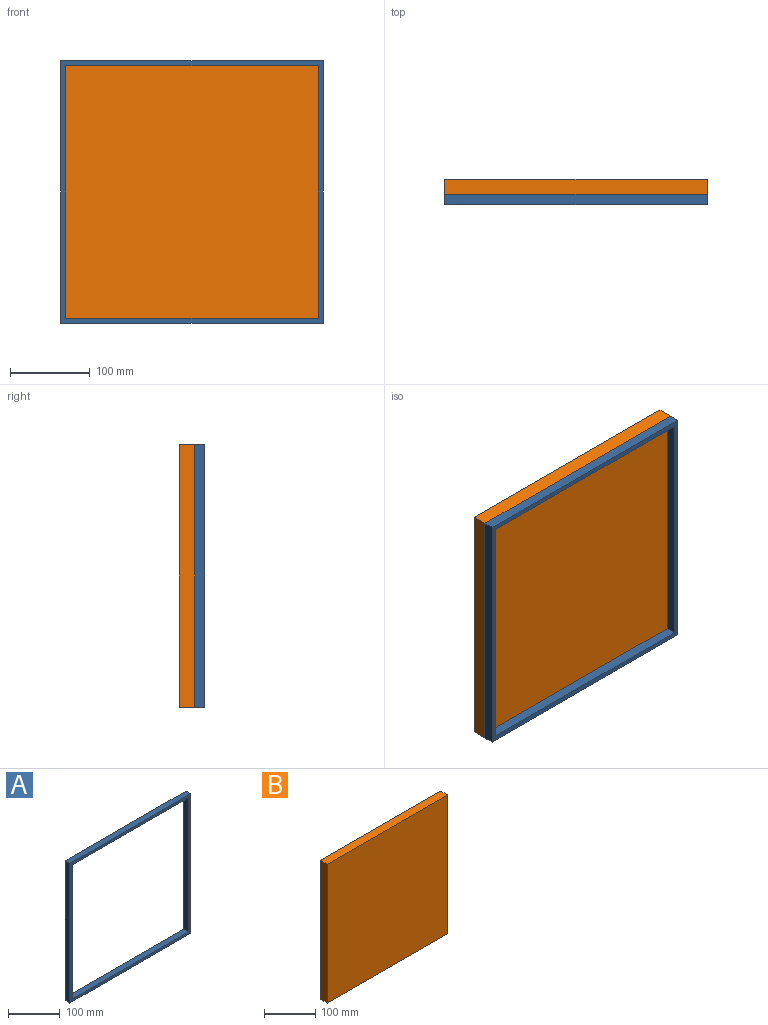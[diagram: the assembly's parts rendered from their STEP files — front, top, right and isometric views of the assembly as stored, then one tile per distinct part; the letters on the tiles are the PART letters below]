
ASSEMBLY  parts=2 mates=1
PART A: 10 faces, bbox 330.2x12.7x330.2 mm
  f0: plane 317.5x12.7mm, normal (0,0,1), area 4032.3mm2, adj f1,f7,f8,f9
  f1: plane 317.5x12.7mm, normal (1,0,0), area 4032.3mm2, adj f0,f2,f8,f9
  f2: plane 317.5x12.7mm, normal (0,0,-1), area 4032.3mm2, adj f1,f7,f8,f9
  f3: plane 330.2x12.7mm, normal (0,0,-1), area 4193.5mm2, adj f4,f6,f8,f9
  f4: plane 330.2x12.7mm, normal (1,0,0), area 4193.5mm2, adj f3,f5,f8,f9
  f5: plane 330.2x12.7mm, normal (0,0,1), area 4193.5mm2, adj f4,f6,f8,f9
  f6: plane 330.2x12.7mm, normal (-1,0,0), area 4193.5mm2, adj f3,f5,f8,f9
  f7: plane 317.5x12.7mm, normal (-1,0,0), area 4032.3mm2, adj f0,f2,f8,f9
  f8: plane 330.2x330.2mm, normal (0,-1,0), area 8225.8mm2, adj f0,f1,f2,f3,f4,f5,f6,f7
  f9: plane 330.2x330.2mm, normal (0,1,0), area 8225.8mm2, adj f0,f1,f2,f3,f4,f5,f6,f7
PART B: 6 faces, bbox 330.2x19.1x330.2 mm
  f0: plane 330.2x19.05mm, normal (0,0,-1), area 6290.3mm2, adj f1,f3,f4,f5
  f1: plane 330.2x19.05mm, normal (1,0,0), area 6290.3mm2, adj f0,f2,f4,f5
  f2: plane 330.2x19.05mm, normal (0,0,1), area 6290.3mm2, adj f1,f3,f4,f5
  f3: plane 330.2x19.05mm, normal (-1,0,0), area 6290.3mm2, adj f0,f2,f4,f5
  f4: plane 330.2x330.2mm, normal (0,-1,0), area 109032mm2, adj f0,f1,f2,f3
  f5: plane 330.2x330.2mm, normal (0,1,0), area 109032mm2, adj f0,f1,f2,f3
PLACE A t=(30.77,491.74,-1073.73)mm
PLACE B t=(30.77,491.74,-1073.73)mm
MATE fastened B.f4 <-> A.f9  axis (0,-1,0) through (165.1,-19.05,165.1)mm
